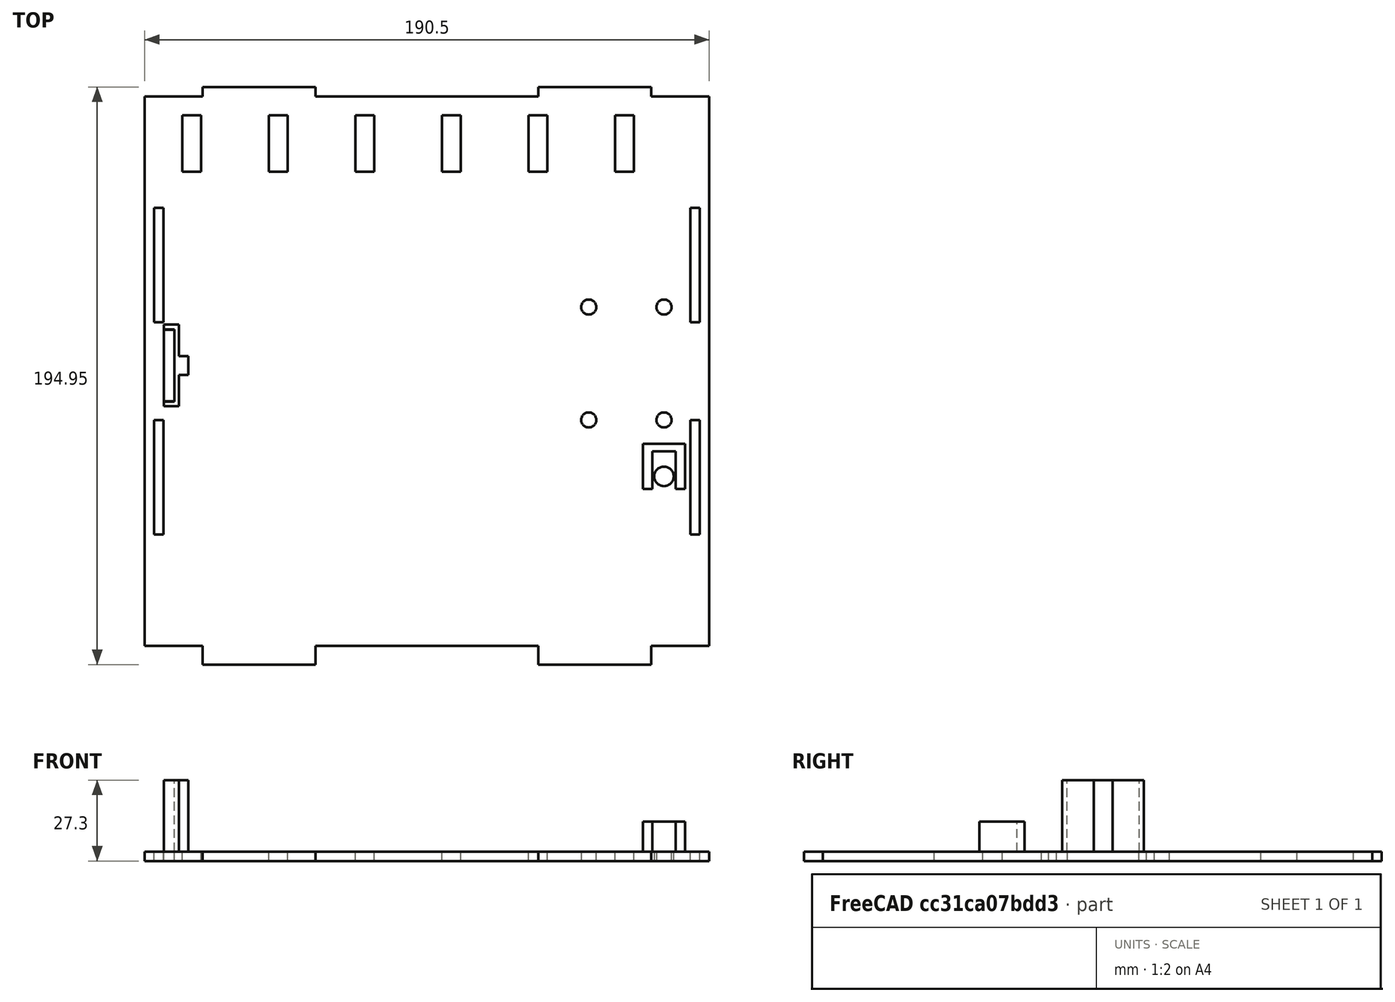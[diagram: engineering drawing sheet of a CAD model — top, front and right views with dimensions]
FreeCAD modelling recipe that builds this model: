
FCSTD DOCUMENT  (FreeCAD 0.18R4 (GitTag))
Label: fpr68k-noresetswitch
License: All rights reserved
LicenseURL: http://en.wikipedia.org/wiki/All_rights_reserved
objects: Sketcher::SketchObject×3, PartDesign::Pad×3, PartDesign::Body×1, App::Part×1, Mesh::Feature×1
note: 10 computed .brp shape members not serialized (recipe doc carries the construction recipe); baked Part::Feature solids carry a one-line shape summary decoded from their .brp

FEATURE [Sketcher::SketchObject] Sketch
  MapMode = 5
  Support = -> [XY_Plane001]
  sketch-geometry (69):
    g0: LineSegment StartX=-132.842 StartY=92.71 StartZ=0 EndX=-113.284 EndY=92.71 EndZ=0
    g1: LineSegment StartX=-113.284 StartY=92.71 StartZ=0 EndX=-113.284 EndY=95.885 EndZ=0
    g2: LineSegment StartX=-113.284 StartY=95.885 StartZ=0 EndX=-75.184 EndY=95.885 EndZ=0
    g3: LineSegment StartX=-75.184 StartY=95.885 StartZ=0 EndX=-75.184 EndY=92.71 EndZ=0
    g4: LineSegment StartX=-75.184 StartY=92.71 StartZ=0 EndX=0 EndY=92.71 EndZ=0
    g5: LineSegment StartX=0 StartY=92.71 StartZ=0 EndX=0 EndY=95.885 EndZ=0
    g6: LineSegment StartX=0 StartY=95.885 StartZ=0 EndX=38.1 EndY=95.885 EndZ=0
    g7: LineSegment StartX=38.1 StartY=95.885 StartZ=0 EndX=38.1 EndY=92.71 EndZ=0
    g8: LineSegment StartX=38.1 StartY=92.71 StartZ=0 EndX=57.658 EndY=92.71 EndZ=0
    g9: LineSegment StartX=57.658 StartY=92.71 StartZ=0 EndX=57.658 EndY=-92.71 EndZ=0
    g10: LineSegment StartX=57.658 StartY=-92.71 StartZ=0 EndX=38.1 EndY=-92.71 EndZ=0
    g11: LineSegment StartX=38.1 StartY=-92.71 StartZ=0 EndX=38.1 EndY=-99.06 EndZ=0
    g12: LineSegment StartX=38.1 StartY=-99.06 StartZ=0 EndX=7.1e-15 EndY=-99.06 EndZ=0
    g13: LineSegment StartX=5.6e-15 StartY=-99.06 StartZ=0 EndX=5.6e-15 EndY=-92.71 EndZ=0
    g14: LineSegment StartX=5.6e-15 StartY=-92.71 StartZ=0 EndX=-75.184 EndY=-92.71 EndZ=0
    g15: LineSegment StartX=-75.184 StartY=-92.71 StartZ=0 EndX=-75.184 EndY=-99.06 EndZ=0
    g16: LineSegment StartX=-75.184 StartY=-99.06 StartZ=0 EndX=-113.284 EndY=-99.06 EndZ=0
    g17: LineSegment StartX=-113.284 StartY=-99.06 StartZ=0 EndX=-113.284 EndY=-92.71 EndZ=0
    g18: LineSegment StartX=-113.284 StartY=-92.71 StartZ=0 EndX=-132.842 EndY=-92.71 EndZ=0
    g19: LineSegment StartX=-132.842 StartY=-92.71 StartZ=0 EndX=-132.842 EndY=92.71 EndZ=0
    g20: LineSegment StartX=-129.718 StartY=55.118 StartZ=0 EndX=-126.441 EndY=55.118 EndZ=0
    g21: LineSegment StartX=-126.441 StartY=55.118 StartZ=0 EndX=-126.441 EndY=16.51 EndZ=0
    g22: LineSegment StartX=-126.441 StartY=16.51 StartZ=0 EndX=-129.718 EndY=16.51 EndZ=0
    g23: LineSegment StartX=-129.718 StartY=16.51 StartZ=0 EndX=-129.718 EndY=55.118 EndZ=0
    g24: LineSegment StartX=51.2572 StartY=55.118 StartZ=0 EndX=54.5338 EndY=55.118 EndZ=0
    g25: LineSegment StartX=54.5338 StartY=55.118 StartZ=0 EndX=54.5338 EndY=16.51 EndZ=0
    g26: LineSegment StartX=54.5338 StartY=16.51 StartZ=0 EndX=51.2572 EndY=16.51 EndZ=0
    g27: LineSegment StartX=51.2572 StartY=16.51 StartZ=0 EndX=51.2572 EndY=55.118 EndZ=0
    g28: LineSegment StartX=51.2572 StartY=-16.51 StartZ=0 EndX=54.5338 EndY=-16.51 EndZ=0
    g29: LineSegment StartX=54.5338 StartY=-16.51 StartZ=0 EndX=54.5338 EndY=-55.118 EndZ=0
    g30: LineSegment StartX=54.5338 StartY=-55.118 StartZ=0 EndX=51.2572 EndY=-55.118 EndZ=0
    g31: LineSegment StartX=51.2572 StartY=-55.118 StartZ=0 EndX=51.2572 EndY=-16.51 EndZ=0
    g32: LineSegment StartX=-129.718 StartY=-16.51 StartZ=0 EndX=-126.441 EndY=-16.51 EndZ=0
    g33: LineSegment StartX=-126.441 StartY=-16.51 StartZ=0 EndX=-126.441 EndY=-55.118 EndZ=0
    g34: LineSegment StartX=-126.441 StartY=-55.118 StartZ=0 EndX=-129.718 EndY=-55.118 EndZ=0
    g35: LineSegment StartX=-129.718 StartY=-55.118 StartZ=0 EndX=-129.718 EndY=-16.51 EndZ=0
    g36: LineSegment StartX=-126.416 StartY=13.97 StartZ=0 EndX=-122.809 EndY=13.97 EndZ=0
    g37: LineSegment StartX=-122.809 StartY=13.97 StartZ=0 EndX=-122.809 EndY=-10.16 EndZ=0
    g38: LineSegment StartX=-122.809 StartY=-10.16 StartZ=0 EndX=-126.416 EndY=-10.16 EndZ=0
    g39: LineSegment StartX=-126.416 StartY=-10.16 StartZ=0 EndX=-126.416 EndY=13.97 EndZ=0
    g40: Circle CenterX=42.418 CenterY=-35.56 CenterZ=0 NormalX=0 NormalY=0 NormalZ=1 AngleXU=0 Radius=3.302
    g41: LineSegment StartX=-120.142 StartY=86.36 StartZ=0 EndX=-113.792 EndY=86.36 EndZ=0
    g42: LineSegment StartX=-113.792 StartY=86.36 StartZ=0 EndX=-113.792 EndY=67.31 EndZ=0
    g43: LineSegment StartX=-113.792 StartY=67.31 StartZ=0 EndX=-120.142 EndY=67.31 EndZ=0
    g44: LineSegment StartX=-120.142 StartY=67.31 StartZ=0 EndX=-120.142 EndY=86.36 EndZ=0
    g45: LineSegment StartX=-84.582 StartY=86.36 StartZ=0 EndX=-90.932 EndY=86.36 EndZ=0
    g46: LineSegment StartX=-90.932 StartY=86.36 StartZ=0 EndX=-90.932 EndY=67.31 EndZ=0
    g47: LineSegment StartX=-90.932 StartY=67.31 StartZ=0 EndX=-84.582 EndY=67.31 EndZ=0
    g48: LineSegment StartX=-84.582 StartY=67.31 StartZ=0 EndX=-84.582 EndY=86.36 EndZ=0
    g49: LineSegment StartX=-61.722 StartY=86.36 StartZ=0 EndX=-55.372 EndY=86.36 EndZ=0
    g50: LineSegment StartX=-55.372 StartY=86.36 StartZ=0 EndX=-55.372 EndY=67.31 EndZ=0
    g51: LineSegment StartX=-55.372 StartY=67.31 StartZ=0 EndX=-61.722 EndY=67.31 EndZ=0
    g52: LineSegment StartX=-61.722 StartY=67.31 StartZ=0 EndX=-61.722 EndY=86.36 EndZ=0
    g53: LineSegment StartX=-32.512 StartY=86.36 StartZ=0 EndX=-26.162 EndY=86.36 EndZ=0
    g54: LineSegment StartX=-26.162 StartY=86.36 StartZ=0 EndX=-26.162 EndY=67.31 EndZ=0
    g55: LineSegment StartX=-26.162 StartY=67.31 StartZ=0 EndX=-32.512 EndY=67.31 EndZ=0
    g56: LineSegment StartX=-32.512 StartY=67.31 StartZ=0 EndX=-32.512 EndY=86.36 EndZ=0
    g57: LineSegment StartX=-3.302 StartY=86.36 StartZ=0 EndX=3.048 EndY=86.36 EndZ=0
    g58: LineSegment StartX=3.048 StartY=86.36 StartZ=0 EndX=3.048 EndY=67.31 EndZ=0
    g59: LineSegment StartX=3.048 StartY=67.31 StartZ=0 EndX=-3.302 EndY=67.31 EndZ=0
    g60: LineSegment StartX=-3.302 StartY=67.31 StartZ=0 EndX=-3.302 EndY=86.36 EndZ=0
    g61: LineSegment StartX=25.908 StartY=86.36 StartZ=0 EndX=32.258 EndY=86.36 EndZ=0
    g62: LineSegment StartX=32.258 StartY=86.36 StartZ=0 EndX=32.258 EndY=67.31 EndZ=0
    g63: LineSegment StartX=32.258 StartY=67.31 StartZ=0 EndX=25.908 EndY=67.31 EndZ=0
    g64: LineSegment StartX=25.908 StartY=67.31 StartZ=0 EndX=25.908 EndY=86.36 EndZ=0
    g65: Circle CenterX=42.418 CenterY=21.59 CenterZ=0 NormalX=0 NormalY=0 NormalZ=1 AngleXU=0 Radius=2.54
    g66: Circle CenterX=17.018 CenterY=21.59 CenterZ=0 NormalX=0 NormalY=0 NormalZ=1 AngleXU=0 Radius=2.54
    g67: Circle CenterX=17.018 CenterY=-16.51 CenterZ=0 NormalX=0 NormalY=0 NormalZ=1 AngleXU=0 Radius=2.54
    g68: Circle CenterX=42.418 CenterY=-16.51 CenterZ=0 NormalX=0 NormalY=0 NormalZ=1 AngleXU=0 Radius=2.54
  constraints (205):
    c: Horizontal(g0)
    c: Coincident(g0,g1)
    c: Vertical(g1)
    c: Coincident(g1,g2)
    c: Horizontal(g2)
    c: Coincident(g2,g3)
    c: Coincident(g3,g4)
    c: Horizontal(g4)
    c: Coincident(g4,g5)
    c: PointOnObject(g5,g-2)
    c: Vertical(g5)
    c: Coincident(g5,g6)
    c: Coincident(g6,g7)
    c: Coincident(g7,g8)
    c: Horizontal(g8)
    c: Coincident(g8,g9)
    c: Coincident(g9,g10)
    c: Horizontal(g10)
    c: Coincident(g10,g11)
    c: Vertical(g11)
    c: Coincident(g11,g12)
    c: Coincident(g12,g13)
    c: Coincident(g13,g14)
    c: Horizontal(g14)
    c: Coincident(g14,g15)
    c: Coincident(g15,g16)
    c: Horizontal(g16)
    c: Coincident(g16,g17)
    c: Coincident(g17,g18)
    c: Horizontal(g18)
    c: Coincident(g18,g19)
    c: Coincident(g19,g0)
    c: Symmetric(g0,g18,g-1)
    c: Symmetric(g8,g9,g-1)
    c: Equal(g9,g19)
    c: DistanceY(g9,g8) = 185.42
    c: Perpendicular(g3,g2)
    c: Perpendicular(g7,g6)
    c: Perpendicular(g13,g12)
    c: Perpendicular(g15,g14)
    c: Equal(g17,g15)
    c: Equal(g15,g13)
    c: Equal(g13,g11)
    c: Equal(g10,g18)
    c: Equal(g18,g0)
    c: Equal(g0,g8)
    c: Equal(g7,g5)
    c: Equal(g5,g3)
    c: Equal(g3,g1)
    c: DistanceX(g10,g9) = 19.558
    c: Equal(g12,g16)
    c: Equal(g16,g2)
    c: Equal(g2,g6)
    c: Equal(g4,g14)
    c: DistanceX(g12,g11) = 38.1
    c: DistanceX(g3,g4) = 75.184
    c: DistanceY(g7,g6) = 3.175
    c: DistanceY(g16,g17) = 6.35
    c: Coincident(g20,g21)
    c: Coincident(g21,g22)
    c: Coincident(g22,g23)
    c: Coincident(g23,g20)
    c: Horizontal(g20)
    c: Horizontal(g22)
    c: Vertical(g21)
    c: Vertical(g23)
    c: DistanceY(g20,g0) = 37.592
    c: DistanceX(g0,g20) = 3.1242
    c: Coincident(g24,g25)
    c: Coincident(g25,g26)
    c: Coincident(g26,g27)
    c: Coincident(g27,g24)
    c: Horizontal(g24)
    c: Horizontal(g26)
    c: Vertical(g25)
    c: Vertical(g27)
    c: DistanceY(g24,g8) = 37.592
    c: DistanceX(g24,g8) = 3.1242
    c: Coincident(g28,g29)
    c: Coincident(g29,g30)
    c: Coincident(g30,g31)
    c: Coincident(g31,g28)
    c: Horizontal(g28)
    c: Horizontal(g30)
    c: Vertical(g29)
    c: Vertical(g31)
    c: DistanceY(g9,g29) = 37.592
    c: DistanceX(g29,g9) = 3.1242
    c: Coincident(g32,g33)
    c: Coincident(g33,g34)
    c: Coincident(g34,g35)
    c: Coincident(g35,g32)
    c: Horizontal(g32)
    c: Horizontal(g34)
    c: Vertical(g33)
    c: Vertical(g35)
    c: DistanceY(g18,g34) = 37.592
    c: DistanceX(g18,g34) = 3.1242
    c: Equal(g33,g31)
    c: Equal(g31,g27)
    c: Equal(g27,g21)
    c: DistanceY(g33,g32) = 38.608
    c: Equal(g28,g26)
    c: Equal(g26,g22)
    c: Equal(g22,g32)
    c: DistanceX(g28,g28) = 3.2766
    c: Coincident(g36,g37)
    c: Coincident(g37,g38)
    c: Coincident(g38,g39)
    c: Coincident(g39,g36)
    c: Horizontal(g36)
    c: Horizontal(g38)
    c: Vertical(g37)
    c: Vertical(g39)
    c: DistanceY(g18,g38) = 82.55
    c: DistanceX(g18,g38) = 6.4262
    c: DistanceY(g37,g36) = 24.13
    c: DistanceX(g38,g37) = 3.6068
    c: Diameter(g40) = 6.604
    c: DistanceY(g9,g40) = 57.15
    c: DistanceX(g40,g9) = 15.24
    c: Coincident(g41,g42)
    c: Coincident(g42,g43)
    c: Coincident(g43,g44)
    c: Coincident(g44,g41)
    c: Horizontal(g41)
    c: Horizontal(g43)
    c: Vertical(g42)
    c: Vertical(g44)
    c: Coincident(g45,g46)
    c: Coincident(g46,g47)
    c: Coincident(g47,g48)
    c: Coincident(g48,g45)
    c: Horizontal(g45)
    c: Horizontal(g47)
    c: Vertical(g46)
    c: Vertical(g48)
    c: Coincident(g49,g50)
    c: Coincident(g50,g51)
    c: Coincident(g51,g52)
    c: Coincident(g52,g49)
    c: Horizontal(g49)
    c: Horizontal(g51)
    c: Vertical(g50)
    c: Vertical(g52)
    c: Coincident(g53,g54)
    c: Coincident(g54,g55)
    c: Coincident(g55,g56)
    c: Coincident(g56,g53)
    c: Horizontal(g53)
    c: Horizontal(g55)
    c: Vertical(g54)
    c: Vertical(g56)
    c: Coincident(g57,g58)
    c: Coincident(g58,g59)
    c: Coincident(g59,g60)
    c: Coincident(g60,g57)
    c: Horizontal(g57)
    c: Horizontal(g59)
    c: Vertical(g58)
    c: Vertical(g60)
    c: Coincident(g61,g62)
    c: Coincident(g62,g63)
    c: Coincident(g63,g64)
    c: Coincident(g64,g61)
    c: Horizontal(g61)
    c: Horizontal(g63)
    c: Vertical(g62)
    c: Vertical(g64)
    c: DistanceX(g61,g8) = 31.75
    c: DistanceY(g61,g8) = 6.35
    c: DistanceX(g53,g57) = 29.21
    c: DistanceX(g57,g61) = 29.21
    c: DistanceX(g49,g53) = 29.21
    c: DistanceX(g45,g49) = 29.21
    c: DistanceX(g41,g45) = 29.21
    c: Equal(g61,g57)
    c: Equal(g57,g53)
    c: Equal(g53,g49)
    c: Equal(g49,g45)
    c: Equal(g45,g41)
    c: DistanceX(g61,g61) = 6.35
    c: DistanceY(g57,g61) = 0
    c: DistanceY(g53,g61) = 0
    c: DistanceY(g49,g61) = 0
    c: DistanceY(g45,g61) = 0
    c: DistanceY(g41,g61) = 0
    c: Equal(g64,g60)
    c: Equal(g60,g56)
    c: Equal(g56,g52)
    c: Equal(g52,g46)
    c: Equal(g46,g44)
    c: DistanceY(g63,g61) = 19.05
    c: Diameter(g65) = 5.08
    c: Equal(g65,g66)
    c: Equal(g65,g67)
    c: Equal(g65,g68)
    c: DistanceX(g66,g65) = 25.4
    c: DistanceX(g67,g68) = 25.4
    c: DistanceY(g67,g66) = 38.1
    c: DistanceY(g68,g65) = 38.1
    c: DistanceY(g66,g65) = 0
    c: DistanceX(g40,g68) = 0
    c: DistanceY(g40,g68) = 19.05
    c: DistanceX(g67,g66) = 0
FEATURE [Sketcher::SketchObject] Sketch001
  MapMode = 5
  Placement = pos=(0,0,3.175) rot=(0,0,1;0rad)
  sketch-geometry (12):
    g0: LineSegment StartX=-126.413 StartY=14.097 StartZ=0 EndX=-122.806 EndY=14.097 EndZ=0
    g1: LineSegment StartX=-122.806 StartY=14.097 StartZ=0 EndX=-122.806 EndY=-10.287 EndZ=0
    g2: LineSegment StartX=-122.806 StartY=-10.287 StartZ=0 EndX=-126.413 EndY=-10.287 EndZ=0
    g3: LineSegment StartX=-126.413 StartY=-10.287 StartZ=0 EndX=-126.413 EndY=-11.8745 EndZ=0
    g4: LineSegment StartX=-126.413 StartY=-11.8745 StartZ=0 EndX=-121.27 EndY=-11.8745 EndZ=0
    g5: LineSegment StartX=-121.27 StartY=-11.8745 StartZ=0 EndX=-121.27 EndY=-1.27 EndZ=0
    g6: LineSegment StartX=-121.27 StartY=-1.27 StartZ=0 EndX=-118.095 EndY=-1.27 EndZ=0
    g7: LineSegment StartX=-118.095 StartY=-1.27 StartZ=0 EndX=-118.095 EndY=5.08 EndZ=0
    g8: LineSegment StartX=-118.095 StartY=5.08 StartZ=0 EndX=-121.27 EndY=5.08 EndZ=0
    g9: LineSegment StartX=-121.27 StartY=5.08 StartZ=0 EndX=-121.27 EndY=15.6845 EndZ=0
    g10: LineSegment StartX=-121.27 StartY=15.6845 StartZ=0 EndX=-126.413 EndY=15.6845 EndZ=0
    g11: LineSegment StartX=-126.413 StartY=15.6845 StartZ=0 EndX=-126.413 EndY=14.097 EndZ=0
  constraints (36):
    c: Horizontal(g0)
    c: Coincident(g0,g1)
    c: Vertical(g1)
    c: Coincident(g1,g2)
    c: Horizontal(g2)
    c: Coincident(g2,g3)
    c: Vertical(g3)
    c: Coincident(g3,g4)
    c: Horizontal(g4)
    c: Coincident(g4,g5)
    c: Vertical(g5)
    c: Coincident(g5,g6)
    c: Coincident(g6,g7)
    c: Coincident(g7,g8)
    c: Coincident(g8,g9)
    c: Vertical(g9)
    c: Coincident(g9,g10)
    c: Coincident(g10,g11)
    c: Coincident(g11,g0)
    c: Perpendicular(g11,g0)
    c: Perpendicular(g10,g11)
    c: Perpendicular(g8,g9)
    c: Perpendicular(g6,g7)
    c: Equal(g11,g3)
    c: Equal(g2,g0)
    c: Equal(g10,g4)
    c: Equal(g9,g5)
    c: Equal(g8,g6)
    c: DistanceY(g6,g7) = 6.35
    c: DistanceY(g1,g0) = 24.384
    c: DistanceX(g10,g9) = 5.1435
    c: DistanceY(g0,g10) = 1.5875
    c: DistanceX(g5,g6) = 3.175
    c: DistanceX(g2,g1) = 3.6068
    c: DistanceX(g7,g-1) = 118.095
    c: DistanceY(g-1,g7) = 5.08
FEATURE [Sketcher::SketchObject] Sketch002
  MapMode = 5
  Placement = pos=(0,-11.8745,3.175) rot=(1,0,0;0rad)
  sketch-geometry (8):
    g0: LineSegment StartX=38.5318 StartY=-27.94 StartZ=0 EndX=35.3568 EndY=-27.94 EndZ=0
    g1: LineSegment StartX=35.3568 StartY=-27.94 StartZ=0 EndX=35.3568 EndY=-12.7 EndZ=0
    g2: LineSegment StartX=35.3568 StartY=-12.7 StartZ=0 EndX=49.5808 EndY=-12.7 EndZ=0
    g3: LineSegment StartX=49.5808 StartY=-12.7 StartZ=0 EndX=49.5808 EndY=-27.94 EndZ=0
    g4: LineSegment StartX=49.5808 StartY=-27.94 StartZ=0 EndX=46.4058 EndY=-27.94 EndZ=0
    g5: LineSegment StartX=46.4058 StartY=-27.94 StartZ=0 EndX=46.4058 EndY=-15.24 EndZ=0
    g6: LineSegment StartX=46.4058 StartY=-15.24 StartZ=0 EndX=38.5318 EndY=-15.24 EndZ=0
    g7: LineSegment StartX=38.5318 StartY=-15.24 StartZ=0 EndX=38.5318 EndY=-27.94 EndZ=0
  constraints (24):
    c: Coincident(g0,g1)
    c: Vertical(g1)
    c: Coincident(g1,g2)
    c: Horizontal(g2)
    c: Coincident(g2,g3)
    c: Vertical(g3)
    c: Coincident(g3,g4)
    c: Coincident(g4,g5)
    c: Vertical(g5)
    c: Coincident(g5,g6)
    c: Horizontal(g6)
    c: Coincident(g6,g7)
    c: Coincident(g7,g0)
    c: Vertical(g7)
    c: Perpendicular(g0,g7)
    c: DistanceY(g0,g6) = 12.7
    c: DistanceY(g0,g1) = 15.24
    c: DistanceX(g6,g5) = 7.874
    c: DistanceX(g0,g0) = 3.175
    c: Equal(g1,g3)
    c: Equal(g7,g5)
    c: Equal(g0,g4)
    c: DistanceX(g-1,g1) = 35.3568
    c: DistanceY(g1,g-1) = 12.7
FEATURE [PartDesign::Pad] Pad
  Length = 3.175
  Length2 = 99.9998
  Profile = -> Sketch
  Type = 0
FEATURE [PartDesign::Pad] Pad001
  BaseFeature = -> Pad
  Length = 24.13
  Length2 = 99.9998
  Profile = -> Sketch001
  Type = 0
FEATURE [PartDesign::Pad] Pad002
  BaseFeature = -> Pad001
  Length = 10.16
  Length2 = 99.9998
  Profile = -> Sketch002
  Type = 0
FEATURE [PartDesign::Body] Body
  Group = -> [Sketch,Sketch001,Sketch002,Pad,Pad001,Pad002]
  Origin = -> Origin001
  Tip = -> Pad002
FEATURE [App::Part] Part
  Group = -> [Body]
  Origin = -> Origin
FEATURE [Mesh::Feature] Mesh  label="fpr68k-noresetswitch"
